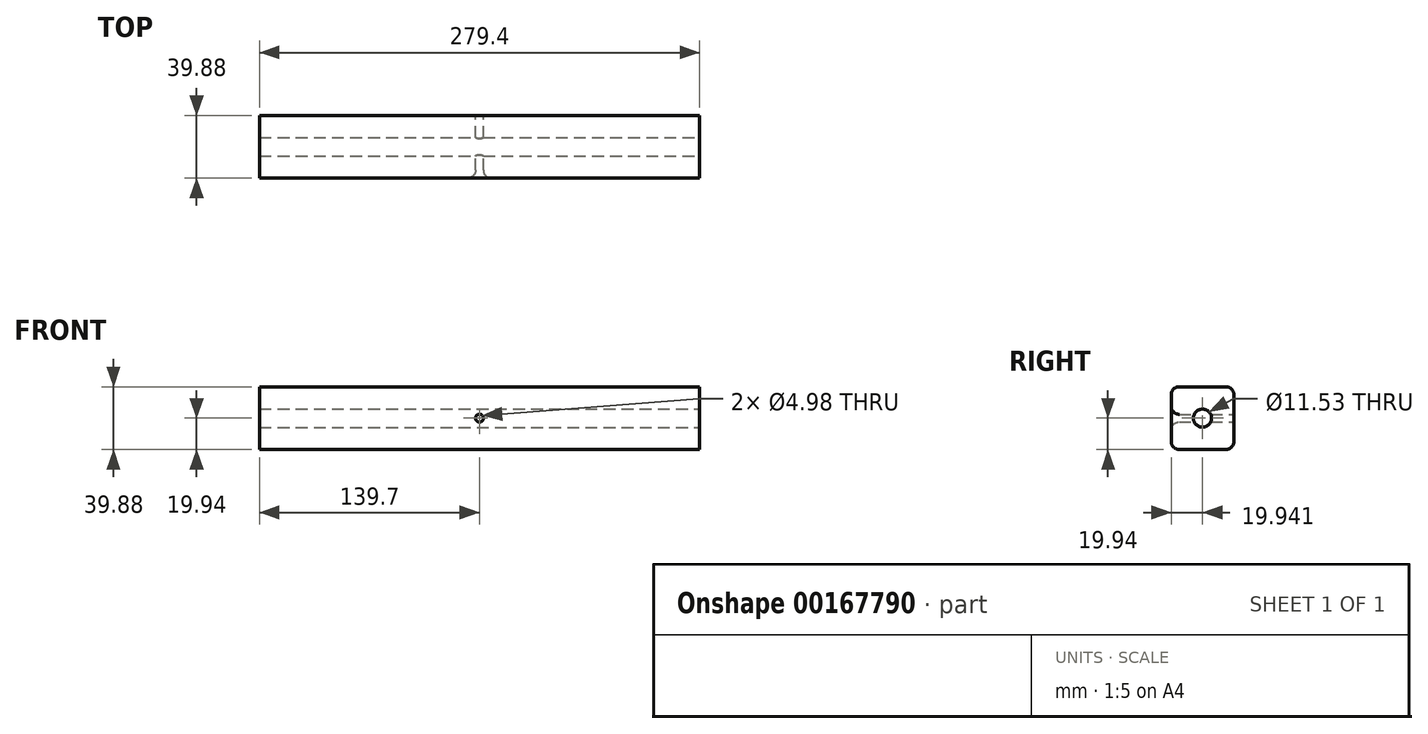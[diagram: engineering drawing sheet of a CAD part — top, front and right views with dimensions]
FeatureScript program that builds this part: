
annotation { "Feature Type Name" : "Feature", "Feature Type Description" : "" }
export const myFeature = defineFeature(function(context is Context, id is Id, definition is map)
    precondition{}
    {
        {
            var Q0;
            Q0=qCreatedBy(makeId("Front.planeOp"),FACE);
            var sketch = newSketch(context, id + "F0", { "sketchPlane" : qUnion([Q0])});
            skLineSegment(sketch, "E0.bottom", {"start": v(139.7, 19.94) * mm, "end": v(-139.7, 19.94) * mm});
            skLineSegment(sketch, "E0.top", {"start": v(139.7, -19.94) * mm, "end": v(-139.7, -19.94) * mm});
            skLineSegment(sketch, "E0.left", {"start": v(139.7, 19.94) * mm, "end": v(139.7, -19.94) * mm});
            skLineSegment(sketch, "E0.right", {"start": v(-139.7, 19.94) * mm, "end": v(-139.7, -19.94) * mm});
            skPoint(sketch, "E0.middle", {"position": v(0, 0) * mm});
            skCircle(sketch, "E1", {"center": v(0, 0) * mm, "radius": 2.49 * mm});
            skLineSegment(sketch, "E2", {"start": v(0, 0) * mm, "end": v(-139.7, 0) * mm});
            skLineSegment(sketch, "E3", {"start": v(0, 0) * mm, "end": v(139.7, 0) * mm});
            skSolve(sketch);
        }
        {
            var Q0;
            Q0=qSketchRegion(id+"F0",true);
            extrude(context, id + "F1", {"entities" : qUnion([Q0]), "depth" : 39.88 * mm});
        }
        {
            var Q0;
            Q0=makeQuery(id+"F1.opExtrude","SWEPT_FACE",FACE,{"disambiguationData":[OSD([sQuery(id+"F0.wireOp",EDGE,"E0.left")])]});
            var sketch = newSketch(context, id + "F2", { "sketchPlane" : qUnion([Q0])});
            skPoint(sketch, "E4.startSnap0", {"position": v(-39.88, 0) * mm});
            skPoint(sketch, "E4.startSnap1", {"position": v(-19.94, 19.94) * mm});
            skCircle(sketch, "E5", {"center": v(-19.94, 0) * mm, "radius": 5.77 * mm});
            skSolve(sketch);
        }
        {
            var Q0;
            Q0=makeQuery(id+"F2.imprint","IMPRINT",FACE,{"disambiguationData":[TD([[makeQuery(id+"F2.imprint","IMPRINT",EDGE,{"derivedFrom":sQuery(id+"F2.wireOp",EDGE,"E5")}),1.0]])]});
            extrude(context, id + "F3", {"entities" : qUnion([Q0]), "operationType" : NewBodyOperationType.REMOVE, "endBound" : BoundingType.THROUGH_ALL, "oppositeDirection" : true, "depth" : 25.4 * mm});
        }
        {
            var Q0;
            Q0=makeQuery(id+"F3.boolean.opBoolean","COPY",EDGE,{"derivedFrom":makeQuery(id+"F3.opExtrude","CAP_EDGE",EDGE,{"disambiguationData":[OSD([sQuery(id+"F2.wireOp",EDGE,"E5")])],"isStart":true})});
            var Q1;
            Q1=makeQuery(id+"F1.opExtrude","CAP_EDGE",EDGE,{"disambiguationData":[OSD([sQuery(id+"F0.wireOp",EDGE,"E1")])],"isStart":false});
            var Q2;
            Q2=makeQuery(id+"F1.opExtrude","CAP_EDGE",EDGE,{"disambiguationData":[OSD([sQuery(id+"F0.wireOp",EDGE,"E0.bottom")])],"isStart":false});
            var Q3;
            Q3=makeQuery(id+"F1.opExtrude","CAP_EDGE",EDGE,{"disambiguationData":[OSD([sQuery(id+"F0.wireOp",EDGE,"E0.bottom")])],"isStart":true});
            var Q4;
            Q4=makeQuery(id+"F1.opExtrude","CAP_EDGE",EDGE,{"disambiguationData":[OSD([sQuery(id+"F0.wireOp",EDGE,"E0.top")])],"isStart":true});
            var Q5;
            Q5=makeQuery(id+"F1.opExtrude","CAP_EDGE",EDGE,{"disambiguationData":[OSD([sQuery(id+"F0.wireOp",EDGE,"E0.top")])],"isStart":false});
            fillet(context, id + "F4", {"entities" : qUnion([Q0, Q1, Q2, Q3, Q4, Q5]), "radius" : 5.08 * mm, "tangentPropagation" : true, "allowEdgeOverflow" : false});
        }
    });
